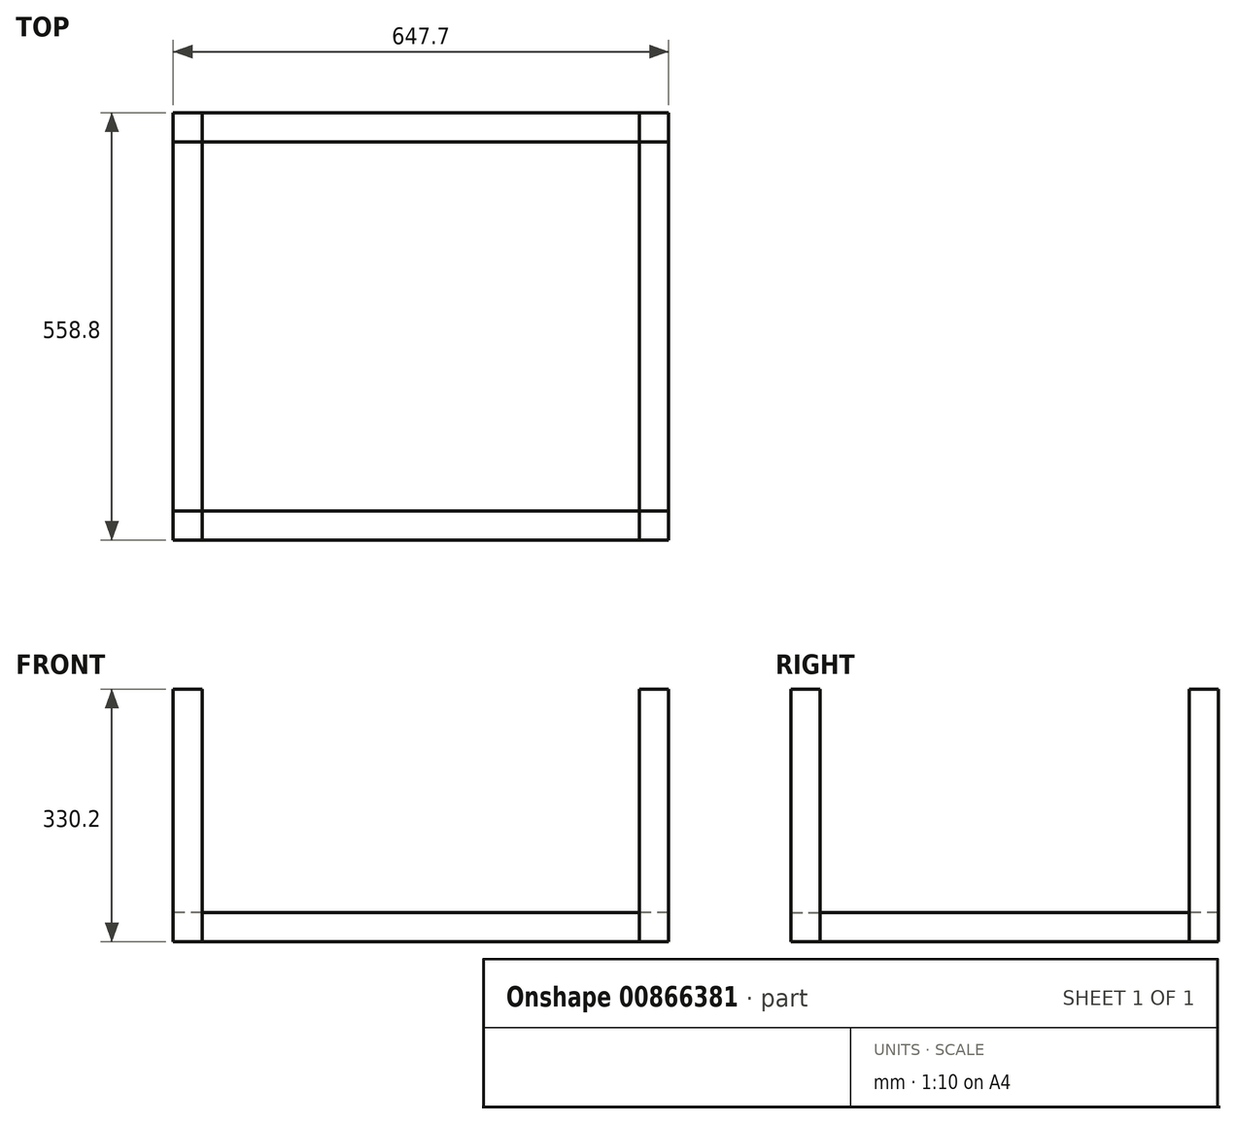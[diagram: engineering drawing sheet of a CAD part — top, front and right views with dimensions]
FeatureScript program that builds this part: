
annotation { "Feature Type Name" : "Feature", "Feature Type Description" : "" }
export const myFeature = defineFeature(function(context is Context, id is Id, definition is map)
    precondition{}
    {
        {
            var Q0;
            Q0=qCreatedBy(makeId("Top.planeOp"),FACE);
            var sketch = newSketch(context, id + "F0", { "sketchPlane" : qUnion([Q0])});
            skLineSegment(sketch, "E0.bottom", {"start": v(-285.75, 241.3) * mm, "end": v(-323.85, 241.3) * mm});
            skLineSegment(sketch, "E0.top", {"start": v(-285.75, -241.3) * mm, "end": v(-323.85, -241.3) * mm});
            skLineSegment(sketch, "E0.left", {"start": v(-285.75, 241.3) * mm, "end": v(-285.75, -241.3) * mm});
            skLineSegment(sketch, "E0.right", {"start": v(-323.85, 241.3) * mm, "end": v(-323.85, -241.3) * mm});
            skPoint(sketch, "E0.middle", {"position": v(-304.8, 0) * mm});
            skLineSegment(sketch, "E1.bottom", {"start": v(323.85, 241.3) * mm, "end": v(285.75, 241.3) * mm});
            skLineSegment(sketch, "E1.top", {"start": v(323.85, -241.3) * mm, "end": v(285.75, -241.3) * mm});
            skLineSegment(sketch, "E1.left", {"start": v(323.85, 241.3) * mm, "end": v(323.85, -241.3) * mm});
            skLineSegment(sketch, "E1.right", {"start": v(285.75, 241.3) * mm, "end": v(285.75, -241.3) * mm});
            skPoint(sketch, "E1.middle", {"position": v(304.8, 0) * mm});
            skLineSegment(sketch, "E2.bottom", {"start": v(285.75, 279.4) * mm, "end": v(-285.75, 279.4) * mm});
            skLineSegment(sketch, "E2.top", {"start": v(285.75, 241.3) * mm, "end": v(-285.75, 241.3) * mm});
            skLineSegment(sketch, "E2.left", {"start": v(285.75, 279.4) * mm, "end": v(285.75, 241.3) * mm});
            skLineSegment(sketch, "E2.right", {"start": v(-285.75, 279.4) * mm, "end": v(-285.75, 241.3) * mm});
            skPoint(sketch, "E2.middle", {"position": v(0, 260.35) * mm});
            skLineSegment(sketch, "E3.bottom", {"start": v(285.75, -279.4) * mm, "end": v(-285.75, -279.4) * mm});
            skLineSegment(sketch, "E3.top", {"start": v(285.75, -241.3) * mm, "end": v(-285.75, -241.3) * mm});
            skLineSegment(sketch, "E3.left", {"start": v(285.75, -279.4) * mm, "end": v(285.75, -241.3) * mm});
            skLineSegment(sketch, "E3.right", {"start": v(-285.75, -279.4) * mm, "end": v(-285.75, -241.3) * mm});
            skPoint(sketch, "E3.middle", {"position": v(0, -260.35) * mm});
            skSolve(sketch);
        }
        {
            var Q0;
            Q0=makeQuery(id+"F0.imprint","IMPRINT",FACE,{"disambiguationData":[TD([[makeQuery(id+"F0.imprint","IMPRINT",EDGE,{"derivedFrom":sQuery(id+"F0.wireOp",EDGE,"E2.bottom")}),1.0]])]});
            var Q1;
            Q1=makeQuery(id+"F0.imprint","IMPRINT",FACE,{"disambiguationData":[TD([[makeQuery(id+"F0.imprint","IMPRINT",EDGE,{"derivedFrom":sQuery(id+"F0.wireOp",EDGE,"E0.bottom")}),1.0]])]});
            var Q2;
            Q2=makeQuery(id+"F0.imprint","IMPRINT",FACE,{"disambiguationData":[TD([[makeQuery(id+"F0.imprint","IMPRINT",EDGE,{"derivedFrom":sQuery(id+"F0.wireOp",EDGE,"E1.bottom")}),1.0]])]});
            var Q3;
            Q3=makeQuery(id+"F0.imprint","IMPRINT",FACE,{"disambiguationData":[TD([[makeQuery(id+"F0.imprint","IMPRINT",EDGE,{"derivedFrom":sQuery(id+"F0.wireOp",EDGE,"E3.bottom")}),-1.0]])]});
            extrude(context, id + "F1", {"entities" : qUnion([Q0, Q1, Q2, Q3]), "depth" : 38.1 * mm, "offsetDistance" : 25.4 * mm});
        }
        {
            var Q0;
            Q0=qCreatedBy(makeId("Top.planeOp"),FACE);
            cPlane(context, id + "F2", {"entities" : qUnion([Q0]), "cplaneType" : CPlaneType.OFFSET, "offset" : 165.1 * mm, "width" : 152.4 * mm, "height" : 152.4 * mm});
        }
        {
            var Q0;
            Q0=qCreatedBy(id+"F2.planeOp",FACE);
            var sketch = newSketch(context, id + "F3", { "sketchPlane" : qUnion([Q0])});
            skLineSegment(sketch, "E4.0", {"start": v(-285.75, 279.4) * mm, "end": v(-285.75, 241.3) * mm});
            skLineSegment(sketch, "E5.0", {"start": v(-285.75, 241.3) * mm, "end": v(-323.85, 241.3) * mm});
            skLineSegment(sketch, "E6.0", {"start": v(285.75, 279.4) * mm, "end": v(285.75, 241.3) * mm});
            skLineSegment(sketch, "E7.0", {"start": v(323.85, 241.3) * mm, "end": v(285.75, 241.3) * mm});
            skLineSegment(sketch, "E8.0", {"start": v(323.85, -241.3) * mm, "end": v(285.75, -241.3) * mm});
            skLineSegment(sketch, "E9.0", {"start": v(285.75, -279.4) * mm, "end": v(285.75, -241.3) * mm});
            skLineSegment(sketch, "E10.0", {"start": v(-285.75, -279.4) * mm, "end": v(-285.75, -241.3) * mm});
            skLineSegment(sketch, "E11.0", {"start": v(-285.75, -241.3) * mm, "end": v(-323.85, -241.3) * mm});
            skLineSegment(sketch, "E12", {"start": v(-285.75, 279.4) * mm, "end": v(-323.85, 279.4) * mm});
            skLineSegment(sketch, "E13", {"start": v(-323.85, 279.4) * mm, "end": v(-323.85, 241.3) * mm});
            skLineSegment(sketch, "E14", {"start": v(-323.85, -241.3) * mm, "end": v(-323.85, -279.4) * mm});
            skLineSegment(sketch, "E15", {"start": v(-323.85, -279.4) * mm, "end": v(-285.75, -279.4) * mm});
            skLineSegment(sketch, "E16", {"start": v(285.75, -279.4) * mm, "end": v(323.85, -279.4) * mm});
            skLineSegment(sketch, "E17", {"start": v(323.85, -279.4) * mm, "end": v(323.85, -241.3) * mm});
            skLineSegment(sketch, "E18", {"start": v(323.85, 241.3) * mm, "end": v(323.85, 279.4) * mm});
            skLineSegment(sketch, "E19", {"start": v(323.85, 279.4) * mm, "end": v(285.75, 279.4) * mm});
            skSolve(sketch);
        }
        {
            var Q0;
            Q0=makeQuery(id+"F3.imprint","IMPRINT",FACE,{"disambiguationData":[TD([[makeQuery(id+"F3.imprint","IMPRINT",EDGE,{"derivedFrom":sQuery(id+"F3.wireOp",EDGE,"E10.0")}),1.0]])]});
            var Q1;
            Q1=makeQuery(id+"F3.imprint","IMPRINT",FACE,{"disambiguationData":[TD([[makeQuery(id+"F3.imprint","IMPRINT",EDGE,{"derivedFrom":sQuery(id+"F3.wireOp",EDGE,"E8.0")}),1.0]])]});
            var Q2;
            Q2=makeQuery(id+"F3.imprint","IMPRINT",FACE,{"disambiguationData":[TD([[makeQuery(id+"F3.imprint","IMPRINT",EDGE,{"derivedFrom":sQuery(id+"F3.wireOp",EDGE,"E6.0")}),1.0]])]});
            var Q3;
            Q3=makeQuery(id+"F3.imprint","IMPRINT",FACE,{"disambiguationData":[TD([[makeQuery(id+"F3.imprint","IMPRINT",EDGE,{"derivedFrom":sQuery(id+"F3.wireOp",EDGE,"E4.0")}),-1.0]])]});
            extrude(context, id + "F4", {"entities" : qUnion([Q0, Q1, Q2, Q3]), "endBound" : BoundingType.SYMMETRIC, "depth" : 330.2 * mm, "offsetDistance" : 25.4 * mm});
        }
    });
